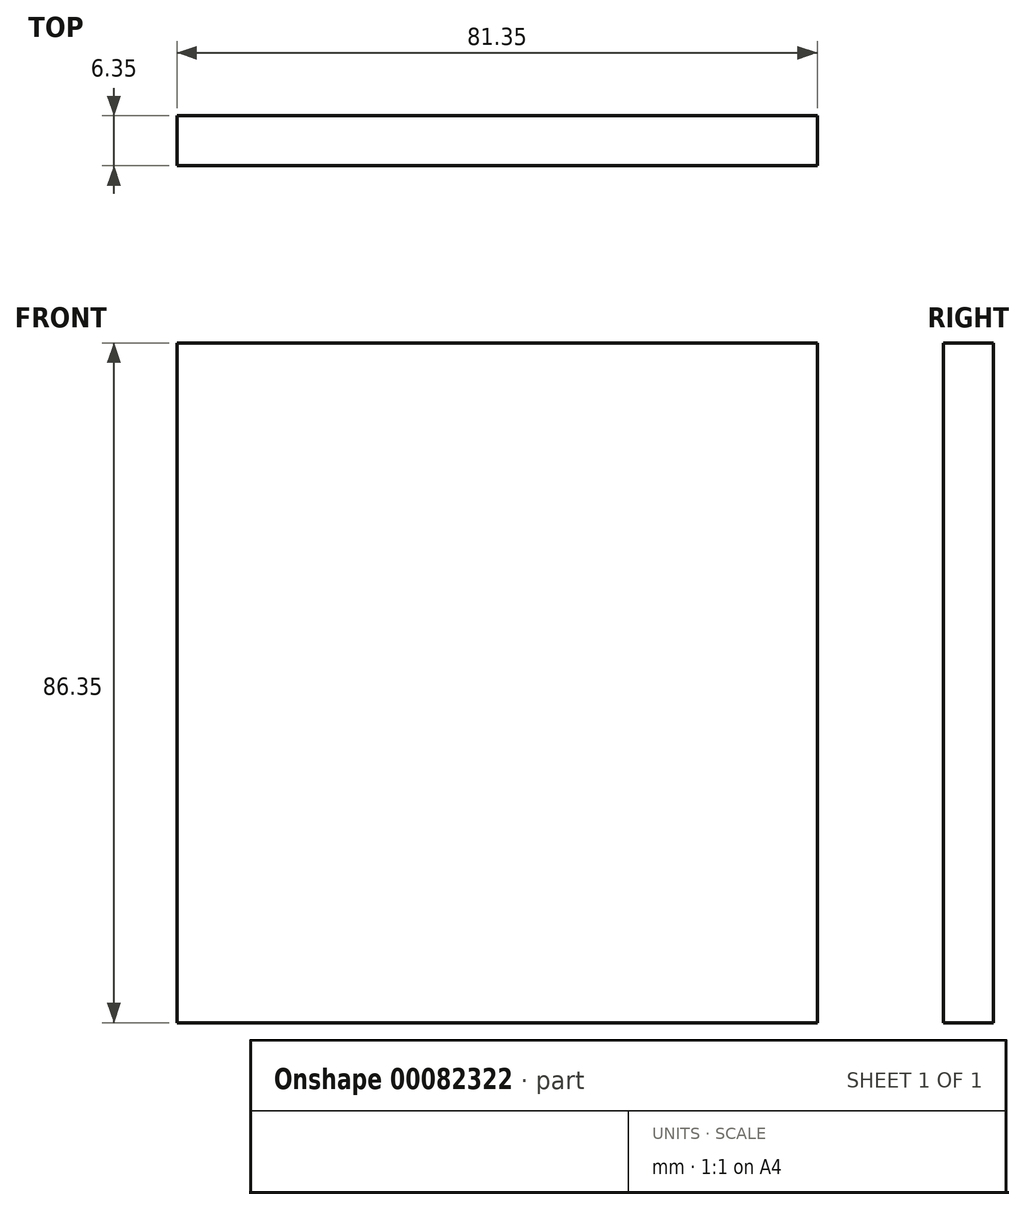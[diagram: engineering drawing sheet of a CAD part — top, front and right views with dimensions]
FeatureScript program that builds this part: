
annotation { "Feature Type Name" : "Feature", "Feature Type Description" : "" }
export const myFeature = defineFeature(function(context is Context, id is Id, definition is map)
    precondition{}
    {
        {
            var Q0;
            Q0=qCreatedBy(makeId("Front.planeOp"),FACE);
            var sketch = newSketch(context, id + "F0", { "sketchPlane" : qUnion([Q0])});
            skLineSegment(sketch, "E0.bottom", {"start": v(37.5, -37.5) * mm, "end": v(-37.5, -37.5) * mm});
            skLineSegment(sketch, "E0.top", {"start": v(37.5, 37.5) * mm, "end": v(-37.5, 37.5) * mm});
            skLineSegment(sketch, "E0.left", {"start": v(37.5, -37.5) * mm, "end": v(37.5, 37.5) * mm});
            skLineSegment(sketch, "E0.right", {"start": v(-37.5, -37.5) * mm, "end": v(-37.5, 37.5) * mm});
            skPoint(sketch, "E0.middle", {"position": v(0, 0) * mm});
            skCircle(sketch, "E1", {"center": v(0, -27.34) * mm, "radius": 5.52 * mm});
            skLineSegment(sketch, "E2.bottom", {"start": v(37.5, 37.5) * mm, "end": v(43.85, 37.5) * mm});
            skLineSegment(sketch, "E2.top", {"start": v(37.5, -43.85) * mm, "end": v(43.85, -43.85) * mm});
            skLineSegment(sketch, "E2.left", {"start": v(37.5, 37.5) * mm, "end": v(37.5, -43.85) * mm});
            skLineSegment(sketch, "E2.right", {"start": v(43.85, 37.5) * mm, "end": v(43.85, -43.85) * mm});
            skLineSegment(sketch, "E3.bottom", {"start": v(-37.5, -37.5) * mm, "end": v(43.85, -37.5) * mm});
            skLineSegment(sketch, "E3.top", {"start": v(-37.5, -43.85) * mm, "end": v(43.85, -43.85) * mm});
            skLineSegment(sketch, "E3.left", {"start": v(-37.5, -37.5) * mm, "end": v(-37.5, -43.85) * mm});
            skLineSegment(sketch, "E3.right", {"start": v(43.85, -37.5) * mm, "end": v(43.85, -43.85) * mm});
            skLineSegment(sketch, "E4.bottom", {"start": v(43.85, 37.5) * mm, "end": v(-37.5, 37.5) * mm});
            skLineSegment(sketch, "E4.top", {"start": v(43.85, 42.5) * mm, "end": v(-37.5, 42.5) * mm});
            skLineSegment(sketch, "E4.left", {"start": v(43.85, 37.5) * mm, "end": v(43.85, 42.5) * mm});
            skLineSegment(sketch, "E4.right", {"start": v(-37.5, 37.5) * mm, "end": v(-37.5, 42.5) * mm});
            skSolve(sketch);
        }
        {
            var Q0;
            {var subQ1=sQuery(id+"F0.wireOp",EDGE,"E0.top");Q0=makeQuery(id+"F0.imprint","IMPRINT",FACE,{"disambiguationData":[TD([[makeQuery(id+"F0.imprint","IMPRINT",EDGE,{"derivedFrom":subQ1}),1.0]])]});}
            var Q1;
            {var subQ0=sQuery(id+"F0.wireOp",EDGE,"E2.bottom");Q1=makeQuery(id+"F0.imprint","IMPRINT",FACE,{"disambiguationData":[TD([[makeQuery(id+"F0.imprint","IMPRINT",EDGE,{"derivedFrom":subQ0}),-1.0]])]});}
            var Q2;
            {var subQ5=sQuery(id+"F0.wireOp",EDGE,"E3.right");Q2=makeQuery(id+"F0.imprint","IMPRINT",FACE,{"disambiguationData":[TD([[makeQuery(id+"F0.imprint","IMPRINT",EDGE,{"derivedFrom":subQ5}),-1.0]])]});}
            var Q3;
            {var subQ5=sQuery(id+"F0.wireOp",EDGE,"E3.left");Q3=makeQuery(id+"F0.imprint","IMPRINT",FACE,{"disambiguationData":[TD([[makeQuery(id+"F0.imprint","IMPRINT",EDGE,{"derivedFrom":subQ5}),1.0]])]});}
            var Q4;
            {var subQ5=sQuery(id+"F0.wireOp",EDGE,"E2.right");Q4=makeQuery(id+"F0.imprint","IMPRINT",FACE,{"disambiguationData":[TD([[makeQuery(id+"F0.imprint","IMPRINT",EDGE,{"derivedFrom":subQ5}),-1.0]])]});}
            var Q5;
            Q5=makeQuery(id+"F0.imprint","IMPRINT",FACE,{"disambiguationData":[TD([[makeQuery(id+"F0.imprint","IMPRINT",EDGE,{"derivedFrom":sQuery(id+"F0.wireOp",EDGE,"E4.top")}),1.0]])]});
            var Q6;
            {var subQ1=sQuery(id+"F0.wireOp",EDGE,"E0.right");Q6=makeQuery(id+"F0.imprint","IMPRINT",FACE,{"disambiguationData":[TD([[makeQuery(id+"F0.imprint","IMPRINT",EDGE,{"derivedFrom":subQ1}),-1.0]])]});}
            var Q7;
            Q7=makeQuery(id+"F0.imprint","IMPRINT",FACE,{"disambiguationData":[TD([[makeQuery(id+"F0.imprint","IMPRINT",EDGE,{"derivedFrom":sQuery(id+"F0.wireOp",EDGE,"E1")}),1.0]])]});
            extrude(context, id + "F1", {"entities" : qUnion([Q0, Q1, Q2, Q3, Q4, Q5, Q6, Q7]), "depth" : 6.35 * mm});
        }
    });
